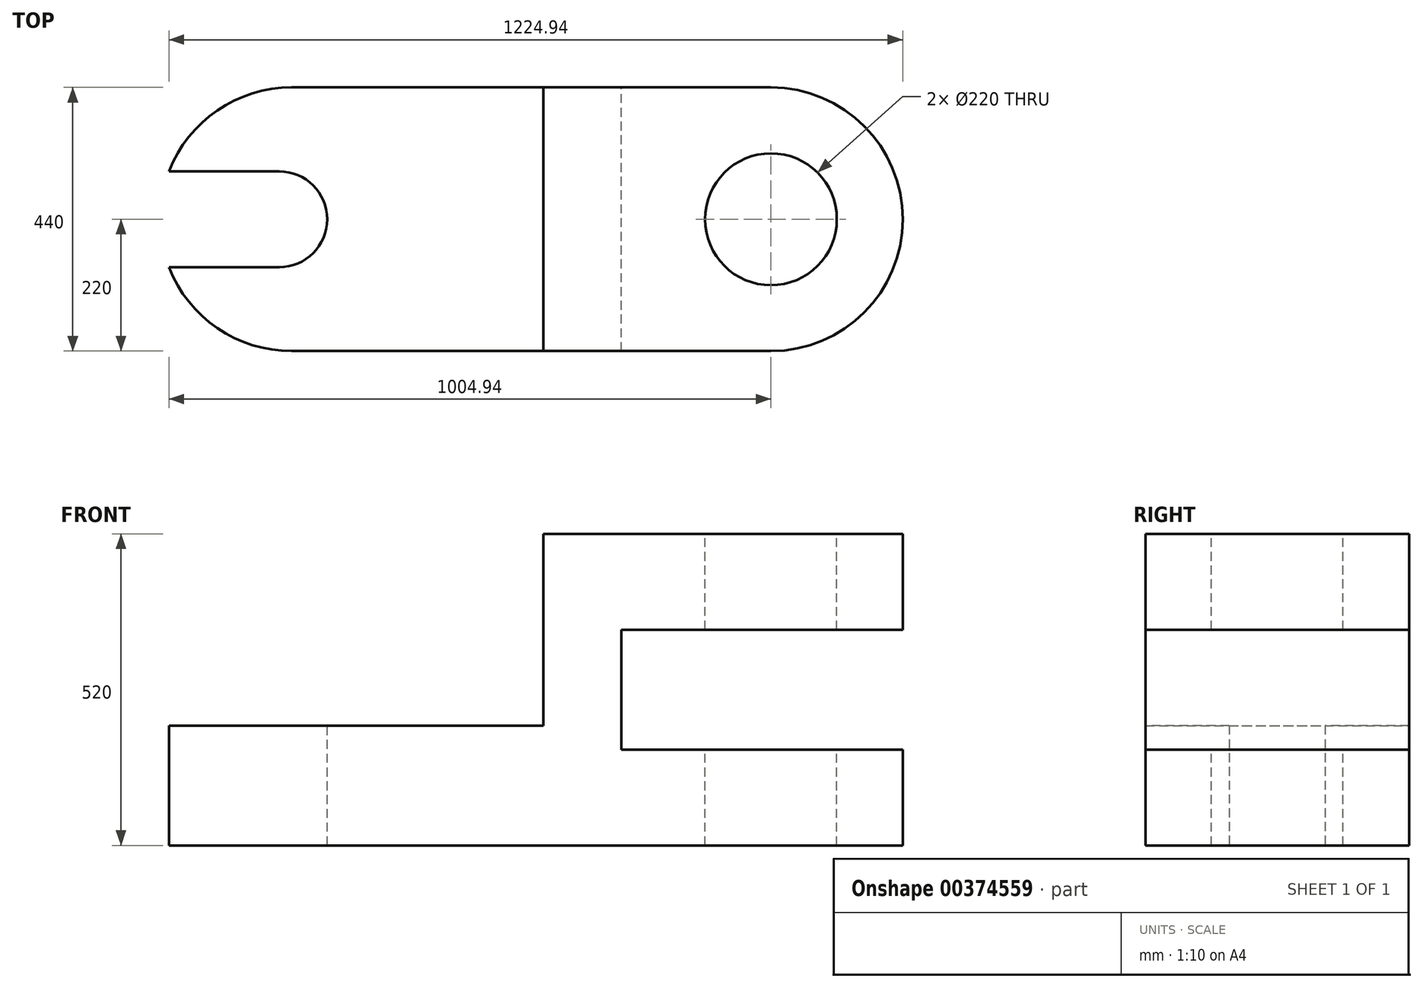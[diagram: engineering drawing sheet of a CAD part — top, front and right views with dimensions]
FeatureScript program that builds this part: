
annotation { "Feature Type Name" : "Feature", "Feature Type Description" : "" }
export const myFeature = defineFeature(function(context is Context, id is Id, definition is map)
    precondition{}
    {
        {
            var Q0;
            Q0=qCreatedBy(makeId("Front.planeOp"),FACE);
            var sketch = newSketch(context, id + "F0", { "sketchPlane" : qUnion([Q0])});
            skLineSegment(sketch, "E0.top", {"start": v(-620, -80) * mm, "end": v(620, -80) * mm});
            skLineSegment(sketch, "E0.right", {"start": v(620, 80) * mm, "end": v(620, -80) * mm});
            skPoint(sketch, "E0.middle", {"position": v(0, 0) * mm});
            skLineSegment(sketch, "E1.top", {"start": v(150, 280) * mm, "end": v(620, 280) * mm});
            skLineSegment(sketch, "E1.right", {"start": v(620, 440) * mm, "end": v(620, 280) * mm});
            skLineSegment(sketch, "E2", {"start": v(150, 80) * mm, "end": v(620, 80) * mm});
            skLineSegment(sketch, "E3", {"start": v(20, 440) * mm, "end": v(20, 120) * mm});
            skLineSegment(sketch, "E4", {"start": v(150, 280) * mm, "end": v(150, 80) * mm});
            skLineSegment(sketch, "E5", {"start": v(20, 440) * mm, "end": v(620, 440) * mm});
            skLineSegment(sketch, "E6", {"start": v(-620, 120) * mm, "end": v(-620, -80) * mm});
            skLineSegment(sketch, "E7.bottom", {"start": v(-420, 120) * mm, "end": v(-280, 120) * mm});
            skLineSegment(sketch, "E7.top", {"start": v(-420, -80) * mm, "end": v(-280, -80) * mm});
            skLineSegment(sketch, "E7.left", {"start": v(-420, 120) * mm, "end": v(-420, -80) * mm});
            skLineSegment(sketch, "E7.right", {"start": v(-280, 120) * mm, "end": v(-280, -80) * mm});
            skLineSegment(sketch, "E8", {"start": v(-620, 120) * mm, "end": v(-420, 120) * mm});
            skLineSegment(sketch, "E9", {"start": v(-280, 120) * mm, "end": v(20, 120) * mm});
            skSolve(sketch);
        }
        {
            var Q0;
            Q0 = qSketchRegion(id + "F0", true);
            extrude(context, id + "F1", {"entities" : qUnion([Q0]), "endBound" : BoundingType.SYMMETRIC, "depth" : 440 * mm});
        }
        {
            var Q0;
            Q0=makeQuery(id+"F1.opExtrude","CAP_EDGE",EDGE,{"disambiguationData":[OSD([sQuery(id+"F0.wireOp",EDGE,"E0.left"),sQuery(id+"F0.wireOp",EDGE,"1kioyjFa-xODz-axkB-xmsr-cUxdMcCwNJlt.left")])],"isStart":true});
            var Q1;
            Q1=makeQuery(id+"F1.opExtrude","CAP_EDGE",EDGE,{"disambiguationData":[OSD([sQuery(id+"F0.wireOp",EDGE,"E0.left"),sQuery(id+"F0.wireOp",EDGE,"1kioyjFa-xODz-axkB-xmsr-cUxdMcCwNJlt.left")])],"isStart":false});
            var Q2;
            Q2=makeQuery(id+"F1.opExtrude","CAP_EDGE",EDGE,{"disambiguationData":[OSD([sQuery(id+"F0.wireOp",EDGE,"E1.right")])],"isStart":true});
            var Q3;
            Q3=makeQuery(id+"F1.opExtrude","CAP_EDGE",EDGE,{"disambiguationData":[OSD([sQuery(id+"F0.wireOp",EDGE,"E1.right")])],"isStart":false});
            var Q4;
            Q4=makeQuery(id+"F1.opExtrude","CAP_EDGE",EDGE,{"disambiguationData":[OSD([sQuery(id+"F0.wireOp",EDGE,"E0.right")])],"isStart":false});
            var Q5;
            Q5=makeQuery(id+"F1.opExtrude","CAP_EDGE",EDGE,{"disambiguationData":[OSD([sQuery(id+"F0.wireOp",EDGE,"E0.right")])],"isStart":true});
            var Q6;
            Q6=makeQuery(id+"F1.opExtrude","CAP_EDGE",EDGE,{"disambiguationData":[OSD([sQuery(id+"F0.wireOp",EDGE,"E6")])],"isStart":true});
            var Q7;
            Q7=makeQuery(id+"F1.opExtrude","CAP_EDGE",EDGE,{"disambiguationData":[OSD([sQuery(id+"F0.wireOp",EDGE,"E6")])],"isStart":false});
            fillet(context, id + "F2", {"entities" : qUnion([Q0, Q1, Q2, Q3, Q4, Q5, Q6, Q7]), "radius" : 220 * mm, "tangentPropagation" : true, "allowEdgeOverflow" : false});
        }
        {
            var Q0;
            Q0=qCreatedBy(makeId("Top.planeOp"),FACE);
            var sketch = newSketch(context, id + "F3", { "sketchPlane" : qUnion([Q0])});
            skCircle(sketch, "E10", {"center": v(-420.85, 0) * mm, "radius": 80 * mm});
            skLineSegment(sketch, "E11.bottom", {"start": v(-420.85, -80) * mm, "end": v(-620.85, -80) * mm});
            skLineSegment(sketch, "E11.top", {"start": v(-420.85, 80) * mm, "end": v(-620.85, 80) * mm});
            skLineSegment(sketch, "E11.left", {"start": v(-420.85, -80) * mm, "end": v(-420.85, 80) * mm});
            skLineSegment(sketch, "E11.right", {"start": v(-620.85, -80) * mm, "end": v(-620.85, 80) * mm});
            skPoint(sketch, "E11.middle", {"position": v(-546.92, 0) * mm});
            skSolve(sketch);
        }
        {
            var Q0;
            Q0 = qSketchRegion(id + "F3", true);
            var Q1;
            Q1=makeQuery(id+"F1.opExtrude","SWEPT_FACE",FACE,{"disambiguationData":[OSD([sQuery(id+"F0.wireOp",EDGE,"E0.top"),sQuery(id+"F0.wireOp",EDGE,"E7.top")])]});
            extrude(context, id + "F4", {"entities" : qUnion([Q0]), "operationType" : NewBodyOperationType.REMOVE, "endBound" : BoundingType.SYMMETRIC, "oppositeDirection" : true, "endBoundEntityFace" : qUnion([Q1]), "depth" : 240 * mm});
        }
        {
            var Q0;
            Q0=qCreatedBy(makeId("Top.planeOp"),FACE);
            var sketch = newSketch(context, id + "F5", { "sketchPlane" : qUnion([Q0])});
            skCircle(sketch, "E12", {"center": v(400, 0) * mm, "radius": 110 * mm});
            skSolve(sketch);
        }
        {
            var Q0;
            Q0 = qSketchRegion(id + "F5", true);
            extrude(context, id + "F6", {"entities" : qUnion([Q0]), "operationType" : NewBodyOperationType.REMOVE, "endBound" : BoundingType.SYMMETRIC, "oppositeDirection" : true, "depth" : 1000 * mm});
        }
    });
